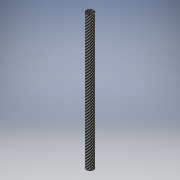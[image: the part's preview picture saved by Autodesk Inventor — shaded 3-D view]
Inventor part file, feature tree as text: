
AUTODESK INVENTOR PART (.ipt)
format: ipt  version: 2018 (Build 220112000, 112)  size: 109,056 bytes
history: native  units: in
note: dims shown in document units (in); Inventor stores cm internally (conversion verified against a paired STEP export)
features: extrude x1, sketch x1
ambient origin geometry x8: Origin, YZ Plane, XZ Plane, XY Plane, X Axis, Y Axis, Z Axis, Center Point
bodies: Solid1 (feature_tree)
feature tree (2):
  extrude  "Extrusion1"  Depth=7.84in
  sketch  "Sketch1"  dims[d0=0.42in d1=0.39in d2=7.84in d3=0.0in]
